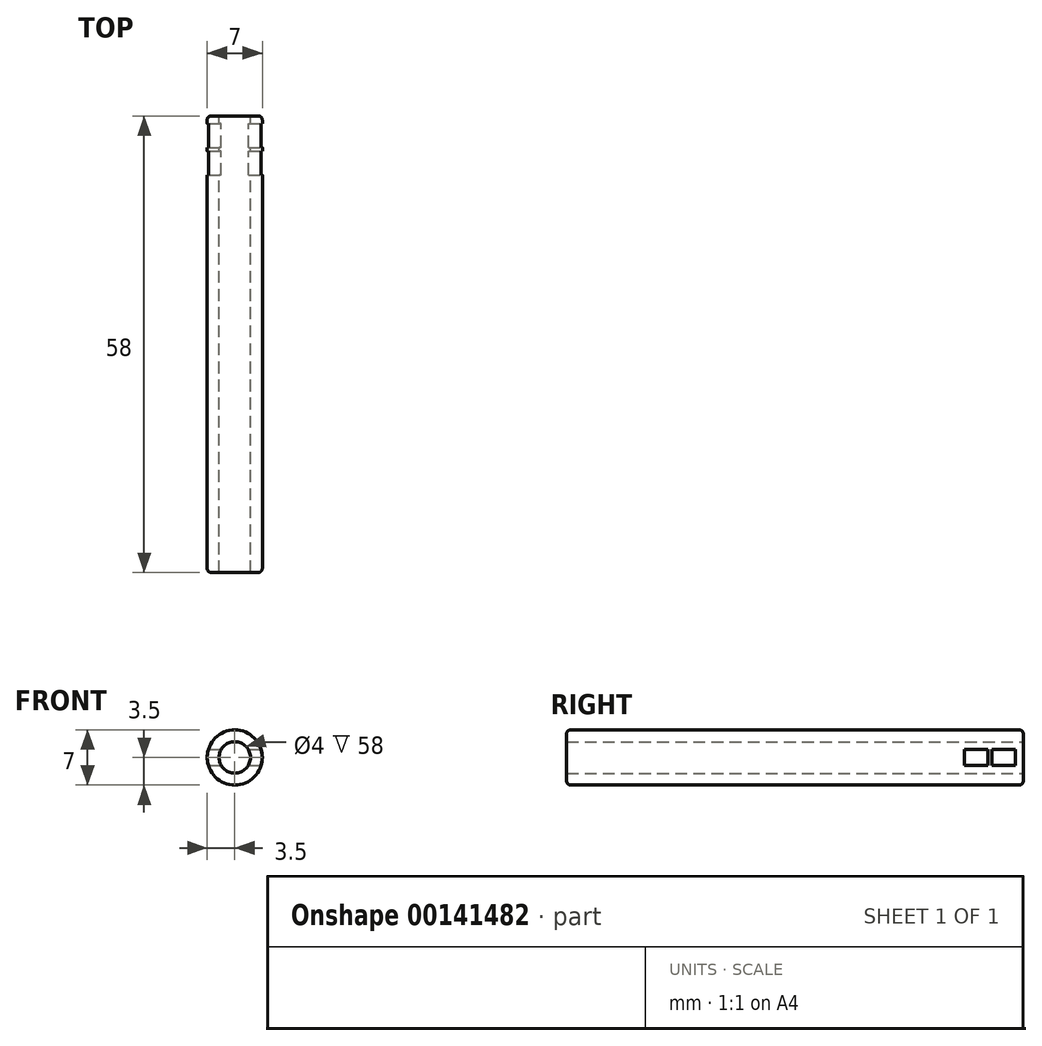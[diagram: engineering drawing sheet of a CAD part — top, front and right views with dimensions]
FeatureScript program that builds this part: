
annotation { "Feature Type Name" : "Feature", "Feature Type Description" : "" }
export const myFeature = defineFeature(function(context is Context, id is Id, definition is map)
    precondition{}
    {
        {
            var Q0;
            Q0=qCreatedBy(makeId("Front.planeOp"),FACE);
            var sketch = newSketch(context, id + "F0", { "sketchPlane" : qUnion([Q0])});
            skCircle(sketch, "E0", {"center": v(0, 0) * mm, "radius": 3.5 * mm});
            skCircle(sketch, "E1", {"center": v(0, 0) * mm, "radius": 2 * mm});
            skSolve(sketch);
        }
        {
            var Q0;
            Q0 = qSketchRegion(id + "F0", true);
            extrude(context, id + "F1", {"entities" : qUnion([Q0]), "depth" : 58 * mm});
        }
        {
            var Q0;
            Q0=makeQuery(id+"F1.opExtrude","CAP_EDGE",EDGE,{"disambiguationData":[OSD([sQuery(id+"F0.wireOp",EDGE,"E0")])],"isStart":false});
            var Q1;
            Q1=makeQuery(id+"F1.opExtrude","CAP_EDGE",EDGE,{"disambiguationData":[OSD([sQuery(id+"F0.wireOp",EDGE,"E0")])],"isStart":true});
            fillet(context, id + "F2", {"entities" : qUnion([Q0, Q1]), "radius" : .5 * mm, "tangentPropagation" : true, "allowEdgeOverflow" : false});
        }
        {
            var Q0;
            Q0=qCreatedBy(makeId("Right.planeOp"),FACE);
            var sketch = newSketch(context, id + "F3", { "sketchPlane" : qUnion([Q0])});
            skLineSegment(sketch, "E2.bottom", {"start": v(-4.5, 1) * mm, "end": v(-7.5, 1) * mm});
            skLineSegment(sketch, "E2.top", {"start": v(-4.5, -1) * mm, "end": v(-7.5, -1) * mm});
            skLineSegment(sketch, "E2.left", {"start": v(-4.5, 1) * mm, "end": v(-4.5, -1) * mm});
            skLineSegment(sketch, "E2.right", {"start": v(-7.5, 1) * mm, "end": v(-7.5, -1) * mm});
            skPoint(sketch, "E2.middle", {"position": v(-6, 0) * mm});
            skLineSegment(sketch, "E3.bottom", {"start": v(-1, 1) * mm, "end": v(-4, 1) * mm});
            skLineSegment(sketch, "E3.top", {"start": v(-1, -1) * mm, "end": v(-4, -1) * mm});
            skLineSegment(sketch, "E3.left", {"start": v(-1, 1) * mm, "end": v(-1, -1) * mm});
            skLineSegment(sketch, "E3.right", {"start": v(-4, 1) * mm, "end": v(-4, -1) * mm});
            skSolve(sketch);
        }
        {
            var Q0;
            Q0 = qSketchRegion(id + "F3", true);
            extrude(context, id + "F4", {"entities" : qUnion([Q0]), "operationType" : NewBodyOperationType.REMOVE, "endBound" : BoundingType.SYMMETRIC, "oppositeDirection" : true, "depth" : 25 * mm});
        }
    });
